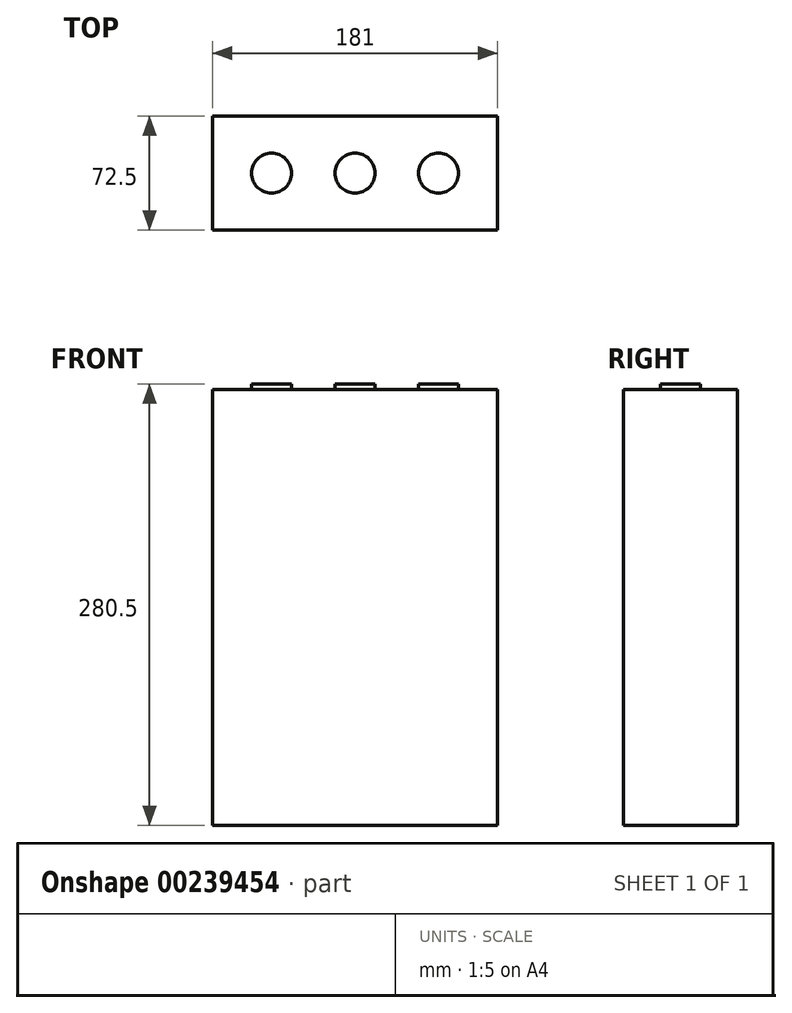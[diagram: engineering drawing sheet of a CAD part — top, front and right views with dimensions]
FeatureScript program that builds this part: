
annotation { "Feature Type Name" : "Feature", "Feature Type Description" : "" }
export const myFeature = defineFeature(function(context is Context, id is Id, definition is map)
    precondition{}
    {
        {
            var Q0;
            Q0=qCreatedBy(makeId("Top.planeOp"),FACE);
            var sketch = newSketch(context, id + "F0", { "sketchPlane" : qUnion([Q0])});
            skLineSegment(sketch, "E0.bottom", {"start": v(-90.5, 72.5) * mm, "end": v(90.5, 72.5) * mm});
            skLineSegment(sketch, "E0.top", {"start": v(-90.5, 0) * mm, "end": v(90.5, 0) * mm});
            skLineSegment(sketch, "E0.left", {"start": v(-90.5, 72.5) * mm, "end": v(-90.5, 0) * mm});
            skLineSegment(sketch, "E0.right", {"start": v(90.5, 72.5) * mm, "end": v(90.5, 0) * mm});
            skSolve(sketch);
        }
        {
            var Q0;
            Q0 = qSketchRegion(id + "F0", true);
            extrude(context, id + "F1", {"entities" : qUnion([Q0]), "depth" : 277 * mm});
        }
        {
            var Q0;
            Q0=makeQuery(id+"F1.opExtrude","CAP_FACE",FACE,{"disambiguationData":[OSD([sQuery(id+"F0.wireOp",EDGE,"E0.bottom"),sQuery(id+"F0.wireOp",EDGE,"E0.top"),sQuery(id+"F0.wireOp",EDGE,"E0.left"),sQuery(id+"F0.wireOp",EDGE,"E0.right")])],"isStart":false});
            var sketch = newSketch(context, id + "F2", { "sketchPlane" : qUnion([Q0])});
            skLineSegment(sketch, "E1", {"start": v(-90.5, 36.25) * mm, "end": v(90.5, 36.25) * mm, "construction": true});
            skCircle(sketch, "E2", {"center": v(-53, 36.25) * mm, "radius": 12.7 * mm});
            skCircle(sketch, "E3", {"center": v(53, 36.25) * mm, "radius": 12.7 * mm});
            skCircle(sketch, "E4", {"center": v(0, 36.25) * mm, "radius": 12.7 * mm});
            skLineSegment(sketch, "E5", {"start": v(0, 36.25) * mm, "end": v(0, 58.69) * mm, "construction": true});
            skSolve(sketch);
        }
        {
            var Q0;
            Q0 = qSketchRegion(id + "F2", true);
            extrude(context, id + "F3", {"entities" : qUnion([Q0]), "depth" : 3.5 * mm});
        }
    });
